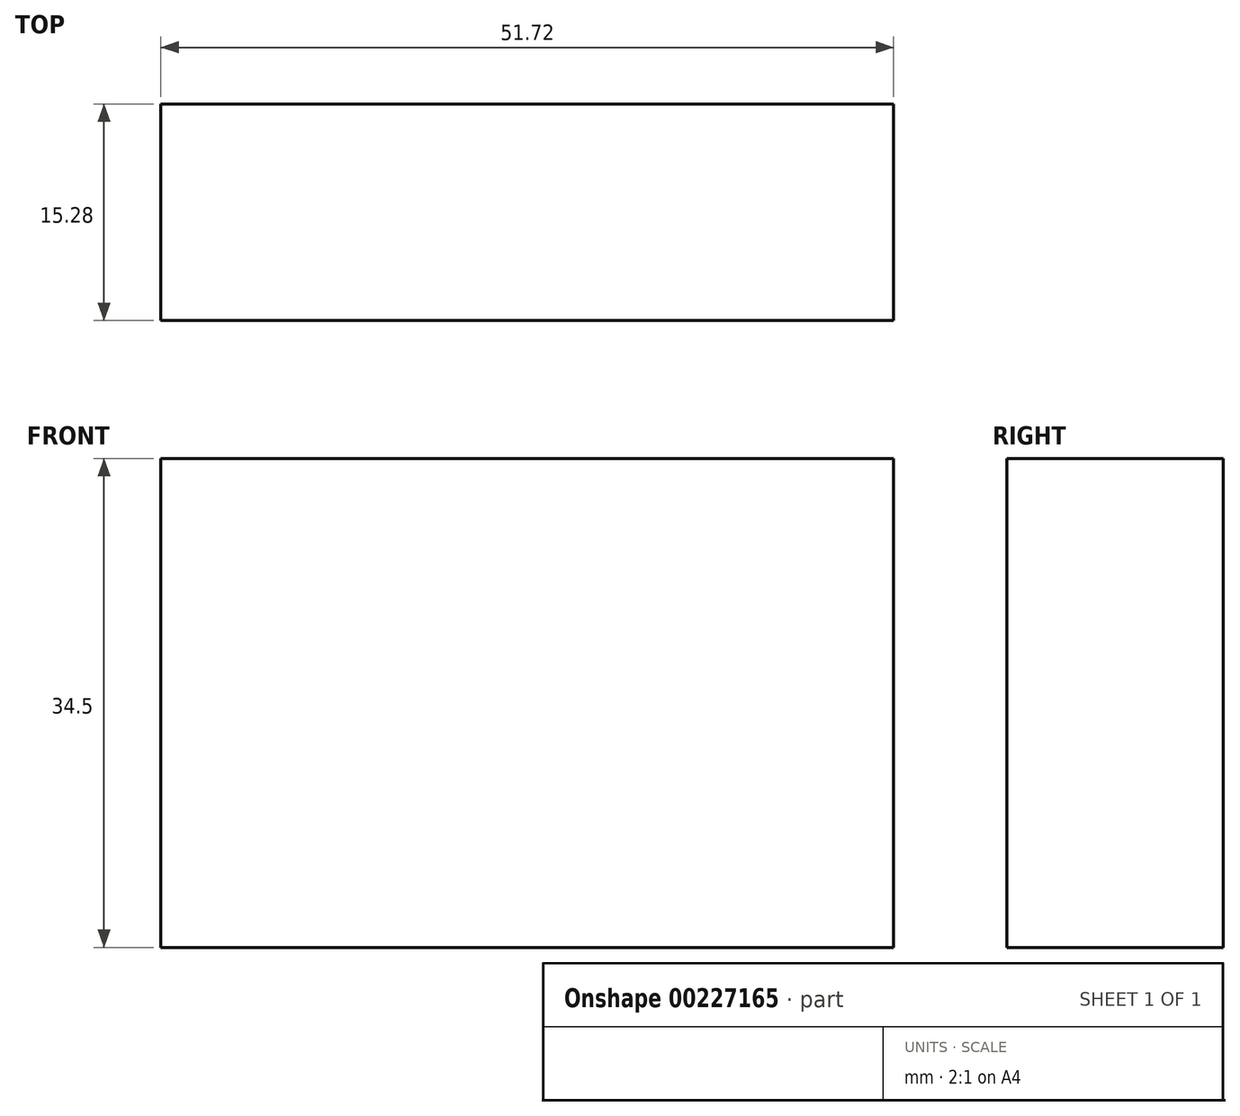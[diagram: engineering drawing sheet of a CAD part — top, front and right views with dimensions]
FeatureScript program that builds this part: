
annotation { "Feature Type Name" : "Feature", "Feature Type Description" : "" }
export const myFeature = defineFeature(function(context is Context, id is Id, definition is map)
    precondition{}
    {
        {
            var Q0;
            Q0=qCreatedBy(makeId("Front.planeOp"),FACE);
            var sketch = newSketch(context, id + "F0", { "sketchPlane" : qUnion([Q0])});
            skLineSegment(sketch, "E0.bottom", {"start": v(25.86, -17.25) * mm, "end": v(-25.86, -17.25) * mm});
            skLineSegment(sketch, "E0.top", {"start": v(25.86, 17.25) * mm, "end": v(-25.86, 17.25) * mm});
            skLineSegment(sketch, "E0.left", {"start": v(25.86, -17.25) * mm, "end": v(25.86, 17.25) * mm});
            skLineSegment(sketch, "E0.right", {"start": v(-25.86, -17.25) * mm, "end": v(-25.86, 17.25) * mm});
            skPoint(sketch, "E0.middle", {"position": v(0, 0) * mm});
            skSolve(sketch);
        }
        {
            var Q0;
            Q0 = qSketchRegion(id + "F0", true);
            extrude(context, id + "F1", {"entities" : qUnion([Q0]), "depth" : 15.28 * mm});
        }
    });
